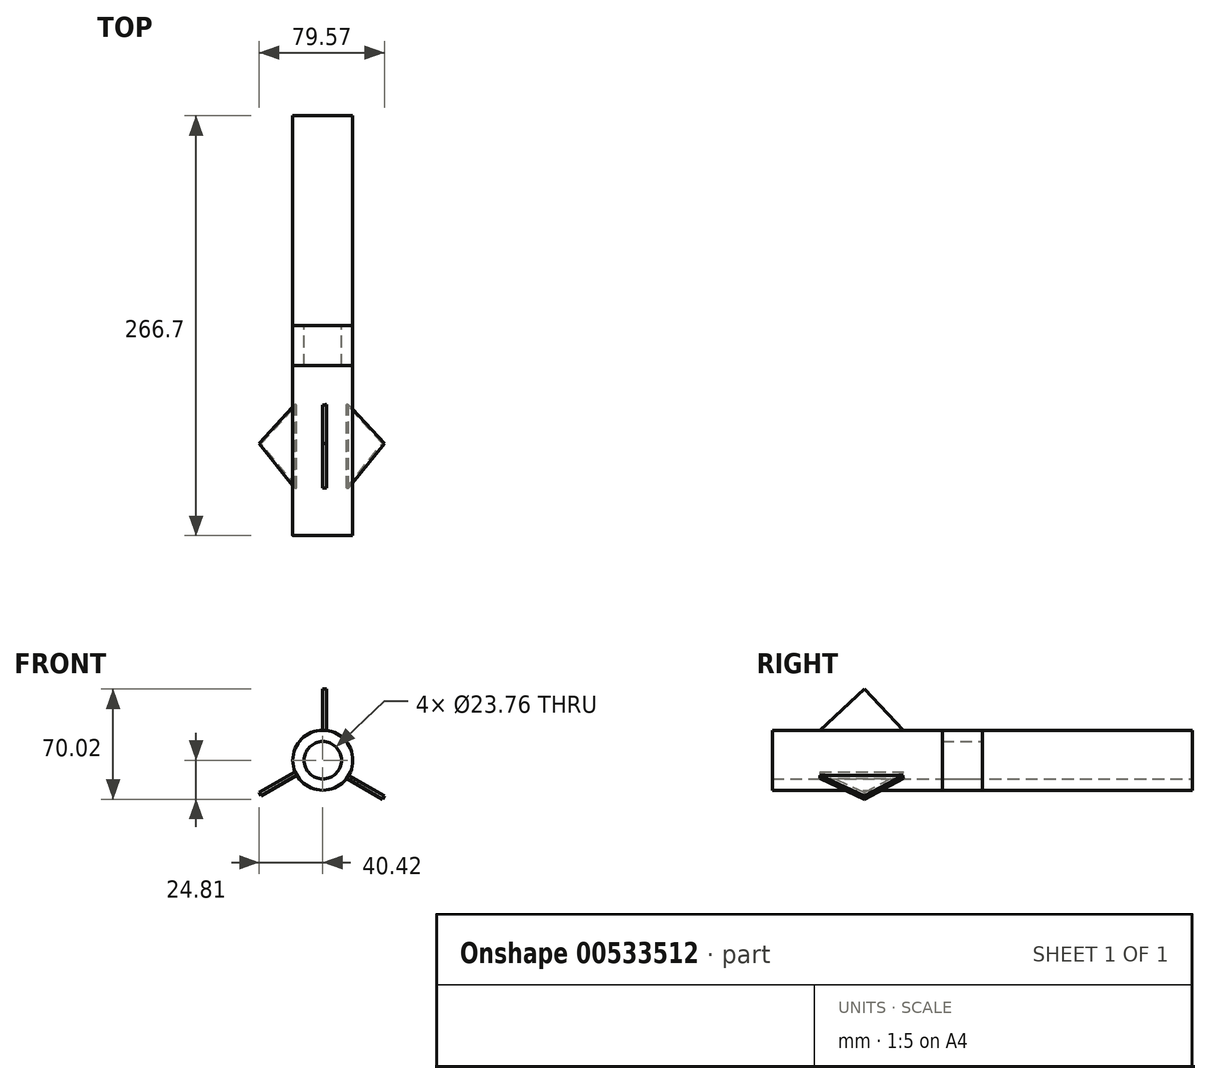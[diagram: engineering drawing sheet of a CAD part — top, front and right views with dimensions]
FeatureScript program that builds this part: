
annotation { "Feature Type Name" : "Feature", "Feature Type Description" : "" }
export const myFeature = defineFeature(function(context is Context, id is Id, definition is map)
    precondition{}
    {
        {
            var Q0;
            Q0=qCreatedBy(makeId("Front.planeOp"),FACE);
            var sketch = newSketch(context, id + "F0", { "sketchPlane" : qUnion([Q0])});
            skCircle(sketch, "E0", {"center": v(0, 0) * mm, "radius": 19.05 * mm});
            skCircle(sketch, "E1", {"center": v(0, 0) * mm, "radius": 11.88 * mm});
            skSolve(sketch);
        }
        {
            var Q0;
            Q0 = qSketchRegion(id + "F0", true);
            extrude(context, id + "F1", {"entities" : qUnion([Q0]), "endBound" : BoundingType.SYMMETRIC, "depth" : 266.7 * mm, "offsetDistance" : 25.4 * mm});
        }
        {
            var Q0;
            Q0=qCreatedBy(makeId("Right.planeOp"),FACE);
            var sketch = newSketch(context, id + "F2", { "sketchPlane" : qUnion([Q0])});
            skLineSegment(sketch, "E2", {"start": v(-107.94, 14.42) * mm, "end": v(-74.83, 45.21) * mm});
            skLineSegment(sketch, "E3", {"start": v(-74.83, 45.21) * mm, "end": v(-44.21, 12.55) * mm});
            skLineSegment(sketch, "E4", {"start": v(-107.94, 14.42) * mm, "end": v(-44.21, 12.55) * mm});
            skLineSegment(sketch, "E5", {"start": v(-74.83, 45.21) * mm, "end": v(-76.07, 13.49) * mm});
            skSolve(sketch);
        }
        {
            var Q0;
            Q0 = qSketchRegion(id + "F2", true);
            extrude(context, id + "F3", {"entities" : qUnion([Q0]), "operationType" : NewBodyOperationType.ADD, "depth" : 2.54 * mm, "offsetDistance" : 25.4 * mm});
        }
        {
            var Q0;
            Q0=makeQuery(id+"F1.opExtrude","SWEPT_BODY",BODY,{"disambiguationData":[OSD([sQuery(id+"F0.wireOp",EDGE,"E0")])]});
            var Q1;
            Q1=makeQuery(id+"F1.opExtrude","CAP_EDGE",EDGE,{"disambiguationData":[OSD([sQuery(id+"F0.wireOp",EDGE,"E0")])],"isStart":false});
            transform(context, id + "F4", {"entities" : qUnion([Q0]), "transformType" : TransformType.ROTATION, "transformAxis" : qUnion([Q1]), "angle" : 240 * degree, "makeCopy" : true});
        }
        {
            var Q0;
            Q0=makeQuery(id+"F1.opExtrude","SWEPT_BODY",BODY,{"disambiguationData":[OSD([sQuery(id+"F0.wireOp",EDGE,"E0")])]});
            var Q1;
            Q1=makeQuery(id+"F1.opExtrude","CAP_EDGE",EDGE,{"disambiguationData":[OSD([sQuery(id+"F0.wireOp",EDGE,"E0")])],"isStart":false});
            transform(context, id + "F5", {"entities" : qUnion([Q0]), "transformType" : TransformType.ROTATION, "transformAxis" : qUnion([Q1]), "angle" : 120 * degree, "makeCopy" : true});
        }
        {
            var Q0;
            Q0 = qSketchRegion(id + "F0", true);
            extrude(context, id + "F6", {"entities" : qUnion([Q0]), "depth" : 25.4 * mm, "offsetDistance" : 25.4 * mm});
        }
    });
